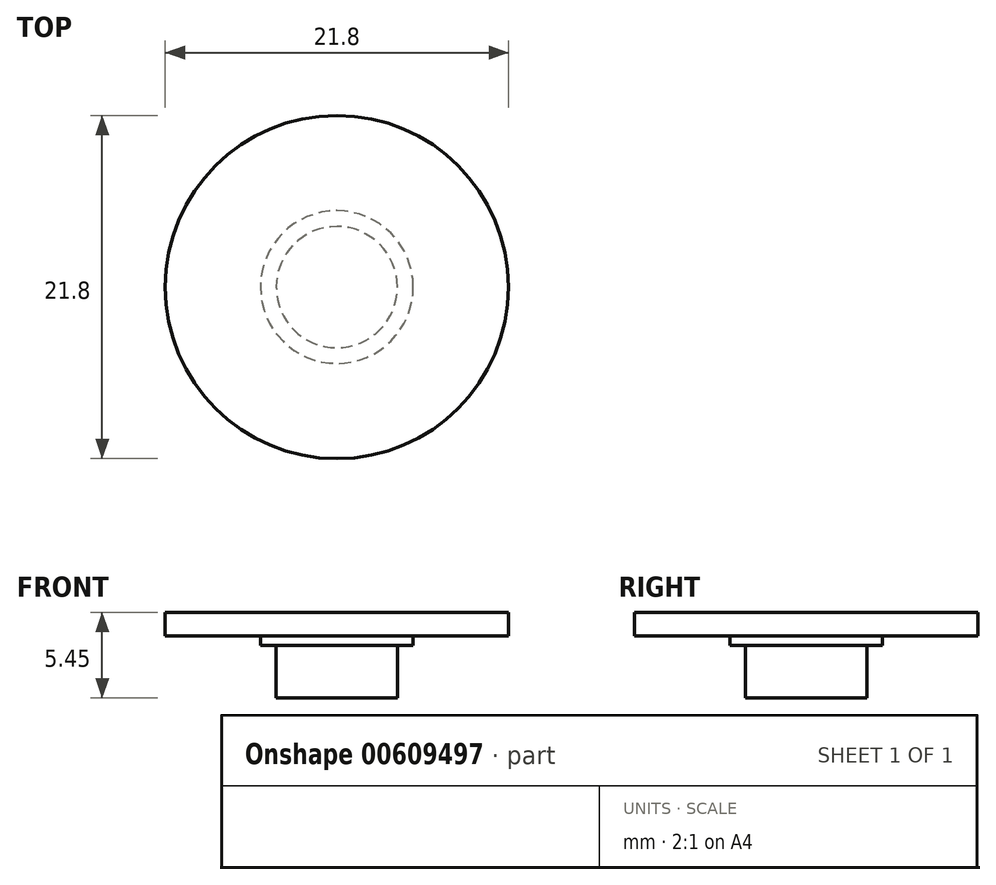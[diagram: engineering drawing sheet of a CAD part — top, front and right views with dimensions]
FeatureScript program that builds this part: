
annotation { "Feature Type Name" : "Feature", "Feature Type Description" : "" }
export const myFeature = defineFeature(function(context is Context, id is Id, definition is map)
    precondition{}
    {
        {
            var Q0;
            Q0=qCreatedBy(makeId("Front.planeOp"),FACE);
            var sketch = newSketch(context, id + "F0", { "sketchPlane" : qUnion([Q0])});
            skLineSegment(sketch, "E0", {"start": v(2.8, 41.19) * mm, "end": v(6.65, 41.19) * mm});
            skLineSegment(sketch, "E1", {"start": v(6.65, 41.19) * mm, "end": v(6.65, 44.54) * mm});
            skLineSegment(sketch, "E2", {"start": v(6.65, 44.54) * mm, "end": v(7.65, 44.54) * mm});
            skLineSegment(sketch, "E3", {"start": v(7.65, 44.54) * mm, "end": v(7.65, 45.14) * mm});
            skLineSegment(sketch, "E4", {"start": v(7.65, 45.14) * mm, "end": v(13.7, 45.14) * mm});
            skLineSegment(sketch, "E5", {"start": v(13.7, 45.14) * mm, "end": v(13.7, 46.64) * mm});
            skLineSegment(sketch, "E6", {"start": v(13.7, 46.64) * mm, "end": v(2.8, 46.64) * mm});
            skLineSegment(sketch, "E7", {"start": v(2.8, 46.64) * mm, "end": v(2.8, 41.19) * mm});
            skLineSegment(sketch, "E8", {"start": v(2.8, 40.6) * mm, "end": v(2.8, 48.57) * mm, "construction": true});
            skSolve(sketch);
        }
        {
            var Q0;
            Q0=makeQuery(id+"F0.imprint","IMPRINT",FACE,{"disambiguationData":[TD([[makeQuery(id+"F0.imprint","IMPRINT",EDGE,{"derivedFrom":sQuery(id+"F0.wireOp",EDGE,"E0")}),1.0]])]});
            var Q1;
            Q1=sQuery(id+"F0.wireOp",EDGE,"E8");
            revolve(context, id + "F1", {"entities" : qUnion([Q0]), "axis" : qUnion([Q1]), "revolveType" : RevolveType.FULL});
        }
    });
